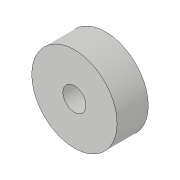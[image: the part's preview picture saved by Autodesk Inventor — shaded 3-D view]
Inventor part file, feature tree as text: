
AUTODESK INVENTOR PART (.ipt)
format: ipt  version: 2018.3 (Build 223284000, 284)  size: 80,896 bytes
history: native  units: in
note: dims shown in document units (in); Inventor stores cm internally (conversion verified against a paired STEP export)
features: extrude x1, sketch x1
ambient origin geometry x8: Origin, YZ Plane, XZ Plane, XY Plane, X Axis, Y Axis, Z Axis, Center Point
bodies: Solid1 (feature_tree)
feature tree (2):
  extrude  "Extrusion1"  Depth=0.251in
  sketch  "Sketch1"  dims[d0=0.186in d1=0.6875in d2=0.251in d3=0.0in]
